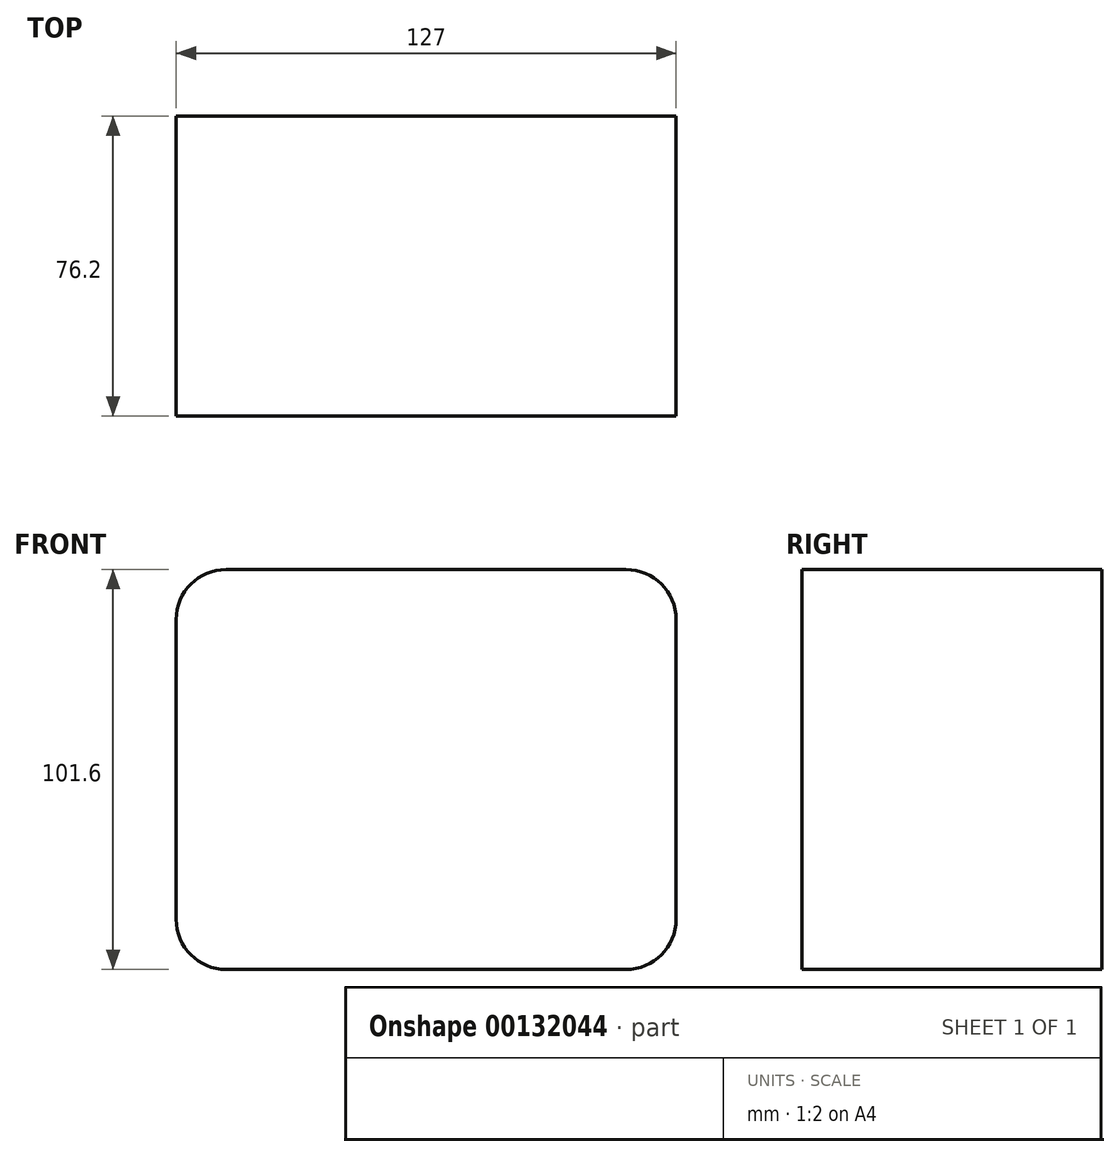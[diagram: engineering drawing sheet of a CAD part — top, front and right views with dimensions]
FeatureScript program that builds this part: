
annotation { "Feature Type Name" : "Feature", "Feature Type Description" : "" }
export const myFeature = defineFeature(function(context is Context, id is Id, definition is map)
    precondition{}
    {
        {
            var Q0;
            Q0=qCreatedBy(makeId("Front.planeOp"),FACE);
            var sketch = newSketch(context, id + "F0", { "sketchPlane" : qUnion([Q0])});
            skLineSegment(sketch, "E0.bottom", {"start": v(-50.8, 50.8) * mm, "end": v(50.8, 50.8) * mm});
            skLineSegment(sketch, "E0.top", {"start": v(-50.8, -50.8) * mm, "end": v(50.8, -50.8) * mm});
            skLineSegment(sketch, "E0.left", {"start": v(-63.5, 38.1) * mm, "end": v(-63.5, -38.1) * mm});
            skLineSegment(sketch, "E0.right", {"start": v(63.5, 38.1) * mm, "end": v(63.5, -38.1) * mm});
            skPoint(sketch, "E1.visualSharp", {"position": v(-63.5, 50.8) * mm});
            skArc(sketch, "E1.filletArc", {"start": v(-50.8, 50.8) * mm, "mid": v(-59.78, 47.08) * mm, "end": v(-63.5, 38.1) * mm});
            skPoint(sketch, "E2.visualSharp", {"position": v(63.5, 50.8) * mm});
            skArc(sketch, "E2.filletArc", {"start": v(63.5, 38.1) * mm, "mid": v(59.78, 47.08) * mm, "end": v(50.8, 50.8) * mm});
            skPoint(sketch, "E3.visualSharp", {"position": v(63.5, -50.8) * mm});
            skArc(sketch, "E3.filletArc", {"start": v(50.8, -50.8) * mm, "mid": v(59.78, -47.08) * mm, "end": v(63.5, -38.1) * mm});
            skPoint(sketch, "E4.visualSharp", {"position": v(-63.5, -50.8) * mm});
            skArc(sketch, "E4.filletArc", {"start": v(-63.5, -38.1) * mm, "mid": v(-59.78, -47.08) * mm, "end": v(-50.8, -50.8) * mm});
            skSolve(sketch);
        }
        {
            var Q0;
            Q0 = qSketchRegion(id + "F0", true);
            extrude(context, id + "F1", {"entities" : qUnion([Q0]), "endBound" : BoundingType.SYMMETRIC, "depth" : 76.2 * mm});
        }
    });
